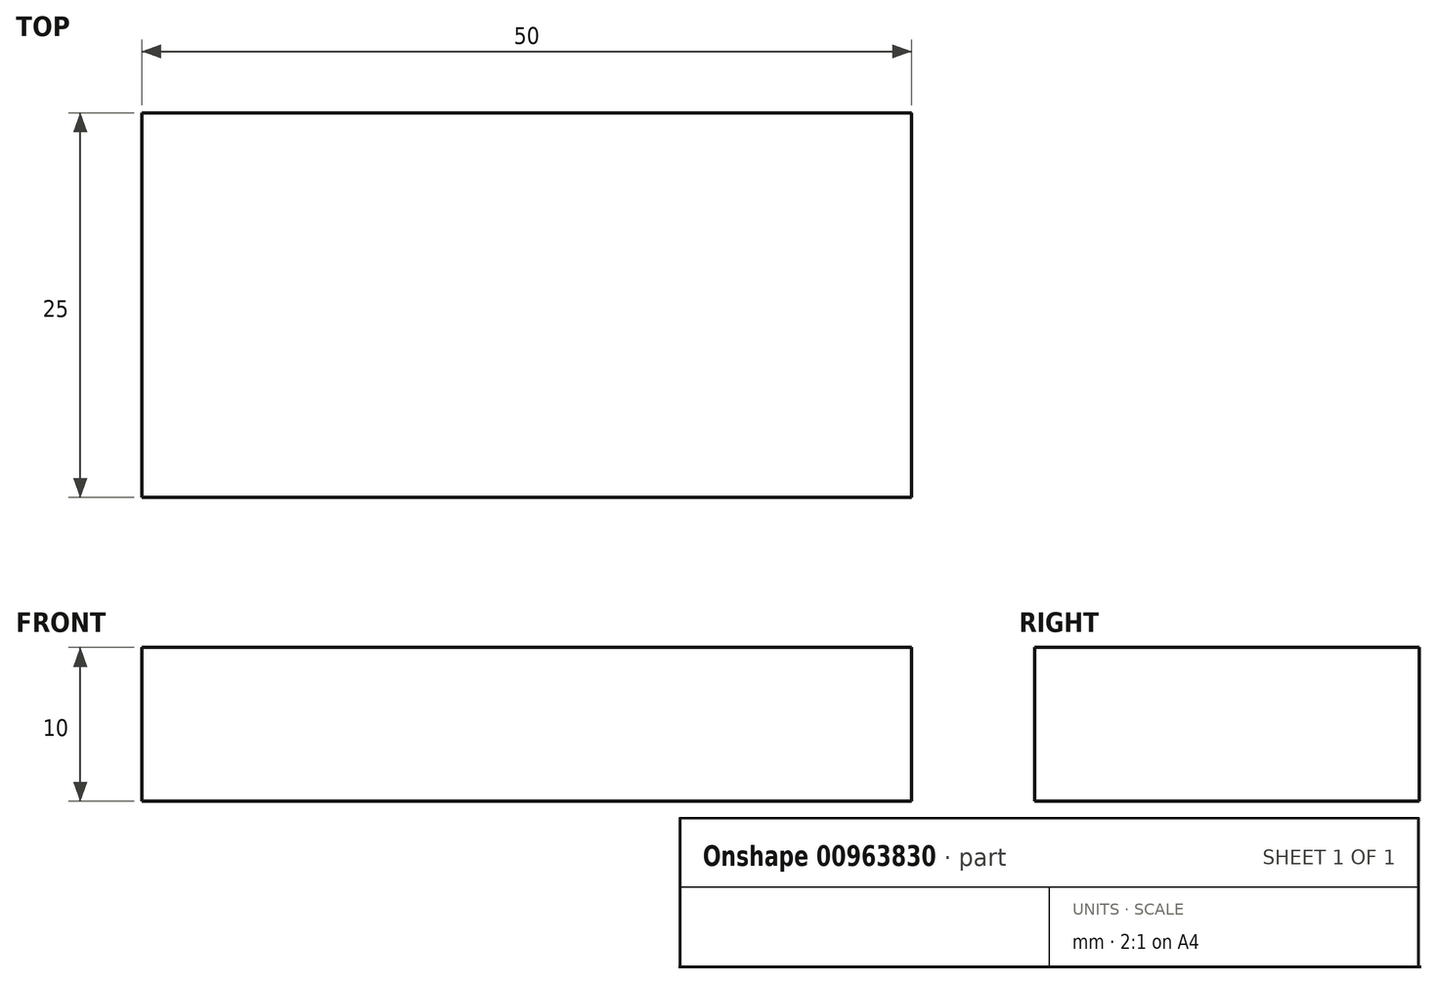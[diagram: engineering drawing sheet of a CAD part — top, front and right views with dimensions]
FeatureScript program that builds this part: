
annotation { "Feature Type Name" : "Feature", "Feature Type Description" : "" }
export const myFeature = defineFeature(function(context is Context, id is Id, definition is map)
    precondition{}
    {
        {
            var Q0;
            Q0=qCreatedBy(makeId("Top.planeOp"),FACE);
            var sketch = newSketch(context, id + "F0", { "sketchPlane" : qUnion([Q0])});
            skLineSegment(sketch, "E0.bottom", {"start": v(-25, 12.5) * mm, "end": v(25, 12.5) * mm});
            skLineSegment(sketch, "E0.top", {"start": v(-25, -12.5) * mm, "end": v(25, -12.5) * mm});
            skLineSegment(sketch, "E0.left", {"start": v(-25, 12.5) * mm, "end": v(-25, -12.5) * mm});
            skLineSegment(sketch, "E0.right", {"start": v(25, 12.5) * mm, "end": v(25, -12.5) * mm});
            skSolve(sketch);
        }
        {
            var Q0;
            Q0=makeQuery(id+"F0.imprint","IMPRINT",FACE,{"disambiguationData":[TD([[makeQuery(id+"F0.imprint","IMPRINT",EDGE,{"derivedFrom":sQuery(id+"F0.wireOp",EDGE,"E0.bottom")}),-1.0]])]});
            extrude(context, id + "F1", {"entities" : qUnion([Q0]), "depth" : 10 * mm, "offsetDistance" : 25.4 * mm});
        }
    });
